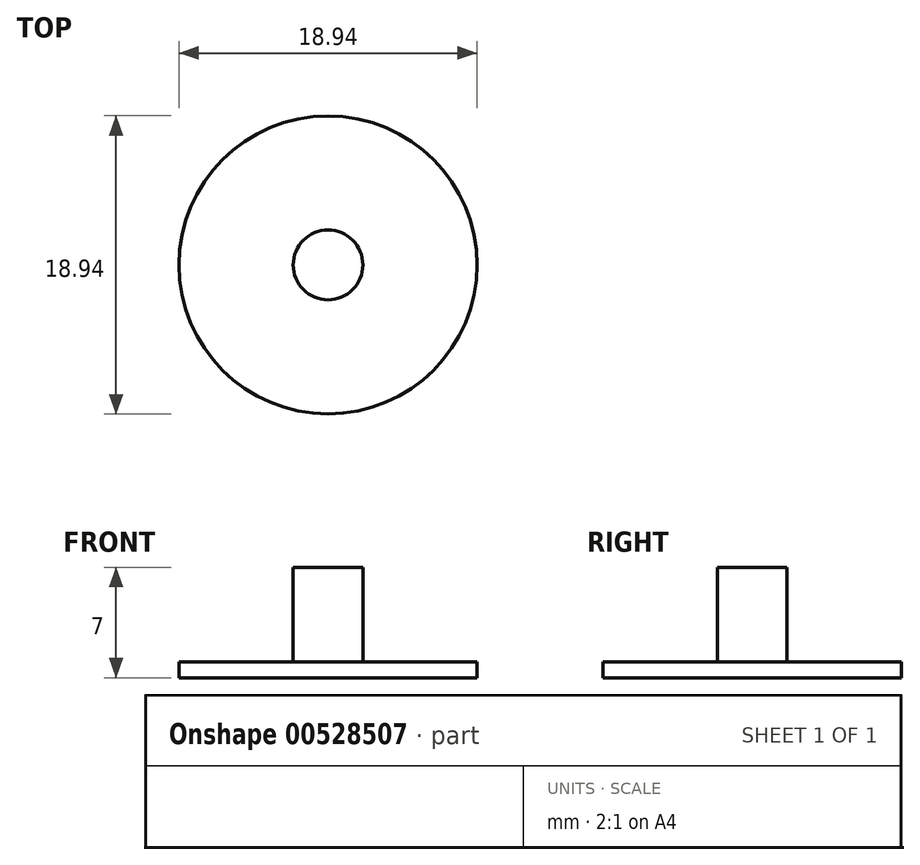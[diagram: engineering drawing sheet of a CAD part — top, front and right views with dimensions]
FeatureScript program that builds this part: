
annotation { "Feature Type Name" : "Feature", "Feature Type Description" : "" }
export const myFeature = defineFeature(function(context is Context, id is Id, definition is map)
    precondition{}
    {
        {
            var Q0;
            Q0=qCreatedBy(makeId("Top.planeOp"),FACE);
            var sketch = newSketch(context, id + "F0", { "sketchPlane" : qUnion([Q0])});
            skCircle(sketch, "E0", {"center": v(0, 0) * mm, "radius": 9.47 * mm});
            skSolve(sketch);
        }
        {
            var Q0;
            Q0=qCreatedBy(makeId("Top.planeOp"),FACE);
            var sketch = newSketch(context, id + "F1", { "sketchPlane" : qUnion([Q0])});
            skCircle(sketch, "E1", {"center": v(0, 0) * mm, "radius": 2.21 * mm});
            skSolve(sketch);
        }
        {
            var Q0;
            Q0=qSketchRegion(id+"F0",true);
            extrude(context, id + "F2", {"entities" : qUnion([Q0]), "depth" : 1 * mm, "offsetDistance" : 25 * mm});
        }
        {
            var Q0;
            Q0 = qSketchRegion(id + "F1", true);
            extrude(context, id + "F3", {"entities" : qUnion([Q0]), "operationType" : NewBodyOperationType.ADD, "depth" : 7 * mm, "offsetDistance" : 25 * mm});
        }
    });
